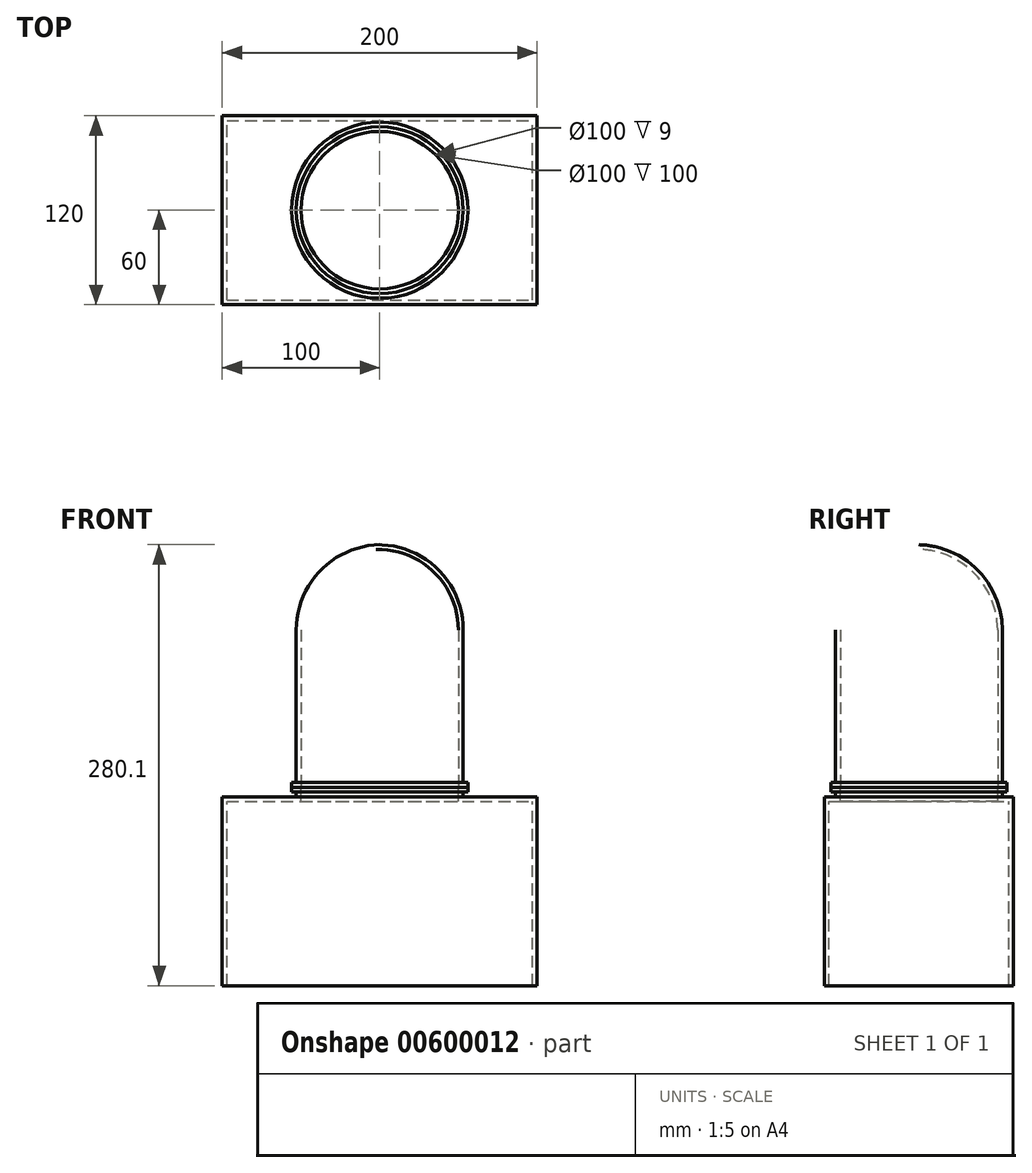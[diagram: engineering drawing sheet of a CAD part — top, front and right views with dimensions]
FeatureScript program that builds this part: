
annotation { "Feature Type Name" : "Feature", "Feature Type Description" : "" }
export const myFeature = defineFeature(function(context is Context, id is Id, definition is map)
    precondition{}
    {
        {
            var Q0;
            Q0=qCreatedBy(makeId("Front.planeOp"),FACE);
            var sketch = newSketch(context, id + "F0", { "sketchPlane" : qUnion([Q0])});
            skLineSegment(sketch, "E0.bottom", {"start": v(-53, 0) * mm, "end": v(-50, 0) * mm});
            skLineSegment(sketch, "E0.top", {"start": v(-53, 100) * mm, "end": v(-50, 100) * mm});
            skLineSegment(sketch, "E0.left", {"start": v(-53, 0) * mm, "end": v(-53, 100) * mm});
            skLineSegment(sketch, "E0.right", {"start": v(-50, 0) * mm, "end": v(-50, 100) * mm});
            skArc(sketch, "E1", {"start": v(-53, 100) * mm, "mid": v(-37.54, 137.86) * mm, "end": v(0, 154.1) * mm});
            skArc(sketch, "E2", {"start": v(-50, 100) * mm, "mid": v(-35.42, 135.74) * mm, "end": v(0, 151.1) * mm});
            skLineSegment(sketch, "E3", {"start": v(0, 154.1) * mm, "end": v(0, 151.1) * mm});
            skLineSegment(sketch, "E4", {"start": v(-53, 0) * mm, "end": v(-56, 0) * mm});
            skLineSegment(sketch, "E5", {"start": v(-56, 0) * mm, "end": v(-56, 3) * mm});
            skLineSegment(sketch, "E6", {"start": v(-56, 3) * mm, "end": v(-53, 3) * mm});
            skLineSegment(sketch, "E7", {"start": v(0, 0) * mm, "end": v(0, 110.42) * mm, "construction": true});
            skSolve(sketch);
        }
        {
            var Q0;
            {var subQ0=sQuery(id+"F0.wireOp",EDGE,"E4");Q0=makeQuery(id+"F0.imprint","IMPRINT",FACE,{"disambiguationData":[TD([[makeQuery(id+"F0.imprint","IMPRINT",EDGE,{"derivedFrom":subQ0}),-1.0]])]});}
            var Q1;
            {var subQ3=sQuery(id+"F0.wireOp",EDGE,"E0.bottom");Q1=makeQuery(id+"F0.imprint","IMPRINT",FACE,{"disambiguationData":[TD([[makeQuery(id+"F0.imprint","IMPRINT",EDGE,{"derivedFrom":subQ3}),1.0]])]});}
            var Q2;
            Q2=makeQuery(id+"F0.imprint","IMPRINT",FACE,{"disambiguationData":[TD([[makeQuery(id+"F0.imprint","IMPRINT",EDGE,{"derivedFrom":sQuery(id+"F0.wireOp",EDGE,"E0.top")}),1.0]])]});
            var Q3;
            Q3=sQuery(id+"F0.wireOp",EDGE,"E7");
            revolve(context, id + "F1", {"entities" : qUnion([Q0, Q1, Q2]), "axis" : qUnion([Q3]), "revolveType" : RevolveType.FULL});
        }
        {
            var Q0;
            Q0=makeQuery(id+"F1.opRevolve","SWEPT_FACE",FACE,{"disambiguationData":[OSD([sQuery(id+"F0.wireOp",EDGE,"E0.bottom"),sQuery(id+"F0.wireOp",EDGE,"E4")])]});
            var sketch = newSketch(context, id + "F2", { "sketchPlane" : qUnion([Q0])});
            skCircle(sketch, "E8", {"center": v(0, 0) * mm, "radius": 50 * mm});
            skPoint(sketch, "E8.first.point", {"position": v(23.05, 44.37) * mm});
            skPoint(sketch, "E8.second.point", {"position": v(40.22, 29.7) * mm});
            skPoint(sketch, "E8.third.point", {"position": v(47.35, 16.06) * mm});
            skCircle(sketch, "E9", {"center": v(0, 0) * mm, "radius": 56 * mm});
            skPoint(sketch, "E9.first.point", {"position": v(21.08, 51.88) * mm});
            skPoint(sketch, "E9.second.point", {"position": v(49.77, 25.67) * mm});
            skPoint(sketch, "E9.third.point", {"position": v(54.42, 13.22) * mm});
            skSolve(sketch);
        }
        {
            var Q0;
            Q0 = qSketchRegion(id + "F2", true);
            extrude(context, id + "F3", {"entities" : qUnion([Q0]), "depth" : 3 * mm, "offsetDistance" : 25 * mm});
        }
        {
            var Q0;
            Q0=makeQuery(id+"F3.opExtrude","CAP_FACE",FACE,{"disambiguationData":[OSD([sQuery(id+"F2.wireOp",EDGE,"E8"),sQuery(id+"F2.wireOp",EDGE,"E9")])],"isStart":false});
            var sketch = newSketch(context, id + "F4", { "sketchPlane" : qUnion([Q0])});
            skCircle(sketch, "E10", {"center": v(0, 0) * mm, "radius": 50 * mm});
            skPoint(sketch, "E10.first.point", {"position": v(-33.66, 36.97) * mm});
            skPoint(sketch, "E10.second.point", {"position": v(41.48, 27.92) * mm});
            skPoint(sketch, "E10.third.point", {"position": v(9.87, -49.02) * mm});
            skCircle(sketch, "E11", {"center": v(0, 0) * mm, "radius": 53 * mm});
            skSolve(sketch);
        }
        {
            var Q0;
            Q0 = qSketchRegion(id + "F4", true);
            extrude(context, id + "F5", {"entities" : qUnion([Q0]), "operationType" : NewBodyOperationType.ADD, "depth" : 3 * mm, "offsetDistance" : 25 * mm});
        }
        {
            var Q0;
            Q0=makeQuery(id+"F5.opExtrude","CAP_FACE",FACE,{"disambiguationData":[OSD([sQuery(id+"F4.wireOp",EDGE,"E10"),sQuery(id+"F4.wireOp",EDGE,"E11")])],"isStart":false});
            var sketch = newSketch(context, id + "F6", { "sketchPlane" : qUnion([Q0])});
            skLineSegment(sketch, "E12.bottom", {"start": v(-100, 60) * mm, "end": v(100, 60) * mm});
            skLineSegment(sketch, "E12.top", {"start": v(-100, -60) * mm, "end": v(100, -60) * mm});
            skLineSegment(sketch, "E12.left", {"start": v(-100, 60) * mm, "end": v(-100, -60) * mm});
            skLineSegment(sketch, "E12.right", {"start": v(100, 60) * mm, "end": v(100, -60) * mm});
            skPoint(sketch, "E12.middle", {"position": v(0, 0) * mm});
            skSolve(sketch);
        }
        {
            var Q0;
            Q0 = qSketchRegion(id + "F6", true);
            extrude(context, id + "F7", {"entities" : qUnion([Q0]), "operationType" : NewBodyOperationType.ADD, "depth" : 120 * mm, "offsetDistance" : 25 * mm});
        }
        {
            var Q0;
            Q0=makeQuery(id+"F7.opExtrude","CAP_FACE",FACE,{"disambiguationData":[OSD([sQuery(id+"F6.wireOp",EDGE,"E12.bottom"),sQuery(id+"F6.wireOp",EDGE,"E12.top"),sQuery(id+"F6.wireOp",EDGE,"E12.left"),sQuery(id+"F6.wireOp",EDGE,"E12.right")])],"isStart":false});
            shell(context, id + "F8", {"entities" : qUnion([Q0]), "thickness" : 3 * mm});
        }
        {
            var Q0;
            Q0=makeQuery(id+"F8.opShell","OFFSET_FACE",FACE,{"disambiguationData":[OSD([sQuery(id+"F6.wireOp",EDGE,"E12.bottom"),sQuery(id+"F6.wireOp",EDGE,"E12.top"),sQuery(id+"F6.wireOp",EDGE,"E12.left"),sQuery(id+"F6.wireOp",EDGE,"E12.right")])]});
            var sketch = newSketch(context, id + "F9", { "sketchPlane" : qUnion([Q0])});
            skCircle(sketch, "E13", {"center": v(0, 0) * mm, "radius": 50 * mm});
            skSolve(sketch);
        }
        {
            var Q0;
            Q0 = qSketchRegion(id + "F9", true);
            extrude(context, id + "F10", {"entities" : qUnion([Q0]), "operationType" : NewBodyOperationType.REMOVE, "oppositeDirection" : true, "depth" : 4 * mm, "offsetDistance" : 25 * mm});
        }
    });
